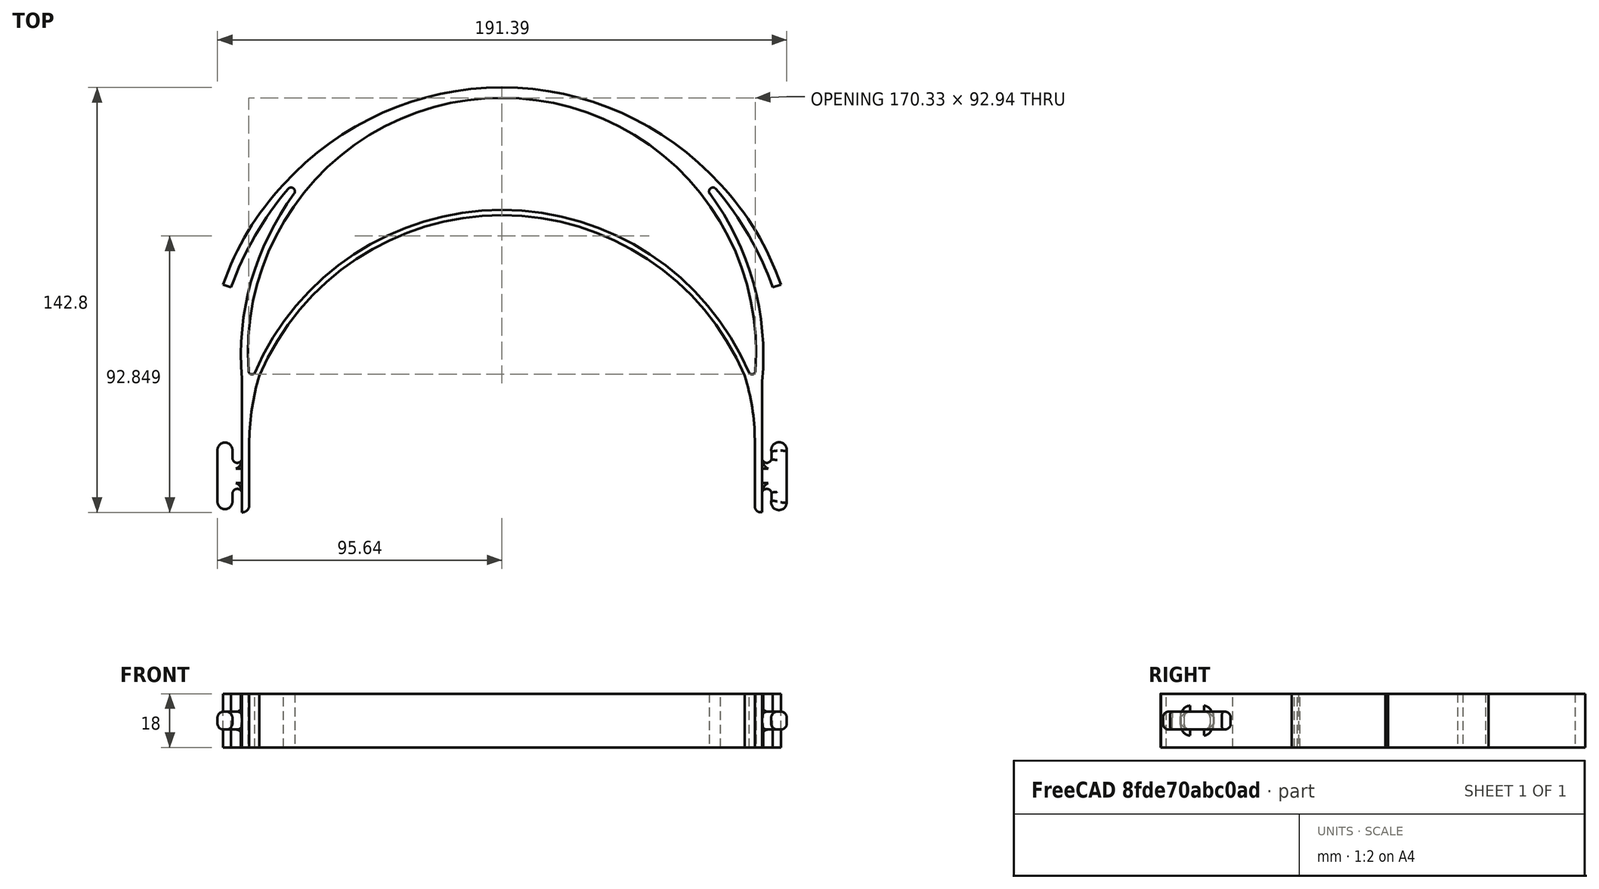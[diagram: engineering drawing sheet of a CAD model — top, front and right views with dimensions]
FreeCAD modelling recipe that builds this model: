
FCSTD DOCUMENT  (FreeCAD 0.18RUnknown)
Label: facemask
License: All rights reserved
LicenseURL: http://en.wikipedia.org/wiki/All_rights_reserved
objects: PartDesign::Fillet×3, Sketcher::SketchObject×2, PartDesign::Pad×2, Mesh::Feature×1, PartDesign::Body×1, App::Part×1
note: 10 computed .brp shape members not serialized (recipe doc carries the construction recipe); baked Part::Feature solids carry a one-line shape summary decoded from their .brp

FEATURE [Mesh::Feature] covid19_headband_rc3
  Placement = pos=(7.8,0,3) rot=(0,0,1;0rad)
FEATURE [Sketcher::SketchObject] Sketch
  sketch-geometry (26):
    g0: ArcOfCircle CenterX=1.5e-15 CenterY=-62.6202 CenterZ=0 NormalX=0 NormalY=0 NormalZ=1 AngleXU=0 Radius=88.7057 StartAngle=0.403137 EndAngle=2.73846
    g1: ArcOfCircle CenterX=0 CenterY=-19.8641 CenterZ=0 NormalX=0 NormalY=0 NormalZ=1 AngleXU=0 Radius=85.4151 StartAngle=6.20691 EndAngle=9.50106
    g2: ArcOfCircle CenterX=1.04e-14 CenterY=-29.9732 CenterZ=0 NormalX=0 NormalY=0 NormalZ=1 AngleXU=0 Radius=99 StartAngle=0.735189 EndAngle=2.4064
    g3: ArcOfCircle CenterX=1.5e-15 CenterY=-62.6202 CenterZ=0 NormalX=0 NormalY=0 NormalZ=1 AngleXU=0 Radius=90.4905 StartAngle=0.405729 EndAngle=2.73586
    g4: ArcOfCircle CenterX=-4.73373 CenterY=-28.0271 CenterZ=0 NormalX=0 NormalY=0 NormalZ=1 AngleXU=0 Radius=94.1996 StartAngle=2.38802 EndAngle=2.80895
    g5: ArcOfCircle CenterX=9.97979 CenterY=-34.403 CenterZ=0 NormalX=0 NormalY=0 NormalZ=1 AngleXU=0 Radius=107.324 StartAngle=2.43909 EndAngle=2.79722
    g6: LineSegment StartX=-93.7694 StartY=2.73342 StartZ=0 EndX=-91.0433 EndY=1.83043 EndZ=0
    g7: ArcOfCircle CenterX=4.73373 CenterY=-28.0271 CenterZ=0 NormalX=0 NormalY=0 NormalZ=1 AngleXU=0 Radius=94.1996 StartAngle=0.332648 EndAngle=0.753573
    g8: ArcOfCircle CenterX=-9.97979 CenterY=-34.403 CenterZ=0 NormalX=0 NormalY=0 NormalZ=1 AngleXU=0 Radius=107.324 StartAngle=0.344373 EndAngle=0.702501
    g9: LineSegment StartX=93.7694 StartY=2.73342 StartZ=0 EndX=91.0433 EndY=1.83043 EndZ=0
    g10: ArcOfCircle CenterX=-84.0634 CenterY=-26.2889 CenterZ=0 NormalX=0 NormalY=0 NormalZ=1 AngleXU=0 Radius=1.10656 StartAngle=3.21787 EndAngle=5.69299
    g11: ArcOfCircle CenterX=84.0634 CenterY=-26.2889 CenterZ=0 NormalX=0 NormalY=0 NormalZ=1 AngleXU=0 Radius=1.10656 StartAngle=3.73179 EndAngle=6.20691
    g12: ArcOfCircle CenterX=3.64266 CenterY=-21.0219 CenterZ=0 NormalX=0 NormalY=0 NormalZ=1 AngleXU=0 Radius=91.4037 StartAngle=2.50512 EndAngle=3.22721
    g13: ArcOfCircle CenterX=-3.52535 CenterY=-21.1802 CenterZ=0 NormalX=0 NormalY=0 NormalZ=1 AngleXU=0 Radius=91.4037 StartAngle=6.18974 EndAngle=6.92181
    g14: ArcOfCircle CenterX=-70.9258 CenterY=34.0894 CenterZ=0 NormalX=0 NormalY=0 NormalZ=1 AngleXU=0 Radius=1.32007 StartAngle=5.64672 EndAngle=8.72228
    g15: ArcOfCircle CenterX=70.9258 CenterY=34.0894 CenterZ=0 NormalX=0 NormalY=0 NormalZ=1 AngleXU=0 Radius=1.32007 StartAngle=0.702501 EndAngle=3.77806
    g16: LineSegment StartX=-87.4263 StartY=-28.8376 StartZ=0 EndX=-87.4263 EndY=-67.5348 EndZ=0
    g17: LineSegment StartX=-87.4263 StartY=-67.5348 StartZ=0 EndX=-87.4263 EndY=-73.7695 EndZ=0
    g18: ArcOfCircle CenterX=-2.80057 CenterY=-51.2587 CenterZ=0 NormalX=0 NormalY=0 NormalZ=1 AngleXU=0 Radius=82.2061 StartAngle=2.85247 EndAngle=3.11992
    g19: ArcOfCircle CenterX=-87.3497 CenterY=-71.3391 CenterZ=0 NormalX=0 NormalY=0 NormalZ=1 AngleXU=0 Radius=2.43161 StartAngle=4.68088 EndAngle=6.04379
    g20: LineSegment StartX=-84.9874 StartY=-49.4774 StartZ=0 EndX=-84.9874 EndY=-71.9157 EndZ=0
    g21: LineSegment StartX=87.4795 StartY=-29.7095 StartZ=0 EndX=87.4795 EndY=-67.711 EndZ=0
    g22: LineSegment StartX=84.9874 StartY=-49.4774 StartZ=0 EndX=84.9874 EndY=-71.9157 EndZ=0
    g23: ArcOfCircle CenterX=11.8888 CenterY=-49.8349 CenterZ=0 NormalX=0 NormalY=0 NormalZ=1 AngleXU=0 Radius=73.0994 StartAngle=0.0048912 EndAngle=0.305907
    g24: LineSegment StartX=87.4795 StartY=-67.711 StartZ=0 EndX=87.4795 EndY=-73.6987 EndZ=0
    g25: ArcOfCircle CenterX=86.9876 CenterY=-71.7531 CenterZ=0 NormalX=0 NormalY=0 NormalZ=1 AngleXU=0 Radius=2.00681 StartAngle=3.22268 EndAngle=4.96003
  constraints (50):
    c: Coincident(g0,g3)
    c: PointOnObject(g1,g-2)
    c: Radius(g2) = 99
    c: Symmetric(g2,g2,g-2)
    c: Coincident(g4,g2)
    c: Coincident(g6,g4)
    c: Coincident(g6,g5)
    c: Coincident(g7,g2)
    c: Coincident(g9,g8)
    c: Equal(g9,g6)
    c: Equal(g5,g8)
    c: Equal(g7,g4)
    c: Symmetric(g5,g8,g-2)
    c: Coincident(g7,g9)
    c: Symmetric(g5,g8,g-2)
    c: Symmetric(g3,g3,g-2)
    c: Symmetric(g0,g0,g-2)
    c: Tangent(g10,g1) = -1.5708
    c: Tangent(g11,g1) = -1.5708
    c: Symmetric(g13,g12,g-2)
    c: Tangent(g14,g5) = -1.5708
    c: Tangent(g14,g12) = 1.5708
    c: Coincident(g15,g8)
    c: Coincident(g15,g13)
    c: Equal(g14,g15)
    c: Symmetric(g4,g7,g-2)
    c: Equal(g11,g10)
    c: Equal(g13,g12)
    c: Coincident(g16,g12)
    c: Vertical(g16)
    c: Vertical(g17)
    c: Coincident(g18,g0)
    c: Coincident(g19,g17)
    c: Coincident(g20,g18)
    c: Coincident(g20,g19)
    c: Vertical(g20)
    c: Coincident(g21,g13)
    c: Vertical(g21)
    c: Vertical(g22)
    c: Coincident(g10,g3)
    c: Coincident(g11,g3)
    c: Equal(g20,g22)
    c: Symmetric(g18,g22,g-2)
    c: Coincident(g23,g0)
    c: Coincident(g23,g22)
    c: Vertical(g24)
    c: Coincident(g25,g24)
    c: Coincident(g25,g22)
    c: Coincident(g17,g16)
    c: Coincident(g24,g21)
FEATURE [PartDesign::Pad] Pad
  Length = 18
  Length2 = 100
  Midplane = true
  Profile = -> Sketch
  Type = 0
FEATURE [Sketcher::SketchObject] Sketch001
  sketch-geometry (16):
    g0: LineSegment StartX=-95.64 StartY=-52.8119 StartZ=0 EndX=-95.64 EndY=-70.2081 EndZ=0
    g1: LineSegment StartX=-90.64 StartY=-67.51 StartZ=0 EndX=-90.64 EndY=-70.2081 EndZ=0
    g2: ArcOfCircle CenterX=-89.01 CenterY=-67.51 CenterZ=0 NormalX=0 NormalY=0 NormalZ=1 AngleXU=0 Radius=1.63 StartAngle=4.87594e-08 EndAngle=3.14159
    g3: ArcOfCircle CenterX=-93.14 CenterY=-70.2081 CenterZ=0 NormalX=0 NormalY=0 NormalZ=1 AngleXU=0 Radius=2.5 StartAngle=3.14159 EndAngle=6.28319
    g4: ArcOfCircle CenterX=-93.14 CenterY=-52.8119 CenterZ=0 NormalX=0 NormalY=0 NormalZ=1 AngleXU=0 Radius=2.5 StartAngle=-9e-16 EndAngle=3.14159
    g5: ArcOfCircle CenterX=-89.01 CenterY=-55.51 CenterZ=0 NormalX=0 NormalY=0 NormalZ=1 AngleXU=0 Radius=1.63 StartAngle=3.14159 EndAngle=6.28319
    g6: LineSegment StartX=-90.64 StartY=-52.8119 StartZ=0 EndX=-90.64 EndY=-55.51 EndZ=0
    g7: LineSegment StartX=95.7222 StartY=-53.1573 StartZ=0 EndX=95.7222 EndY=-70.5535 EndZ=0
    g8: LineSegment StartX=90.575 StartY=-53.2678 StartZ=0 EndX=90.575 EndY=-55.9659 EndZ=0
    g9: LineSegment StartX=90.5881 StartY=-67.102 StartZ=0 EndX=90.5881 EndY=-69.8001 EndZ=0
    g10: ArcOfCircle CenterX=89.01 CenterY=-67.51 CenterZ=0 NormalX=0 NormalY=0 NormalZ=1 AngleXU=0 Radius=1.63 StartAngle=0.253014 EndAngle=3.14159
    g11: ArcOfCircle CenterX=89.01 CenterY=-55.51 CenterZ=0 NormalX=0 NormalY=0 NormalZ=1 AngleXU=0 Radius=1.63 StartAngle=3.14159 EndAngle=5.99972
    g12: ArcOfCircle CenterX=93.14 CenterY=-52.8119 CenterZ=0 NormalX=0 NormalY=0 NormalZ=1 AngleXU=0 Radius=2.60524 StartAngle=6.15021 EndAngle=9.60067
    g13: ArcOfCircle CenterX=93.121 CenterY=-70.4099 CenterZ=0 NormalX=0 NormalY=0 NormalZ=1 AngleXU=0 Radius=2.60524 StartAngle=2.9053 EndAngle=6.22805
    g14: LineSegment StartX=-87.38 StartY=-55.51 StartZ=0 EndX=-87.38 EndY=-67.51 EndZ=0
    g15: LineSegment StartX=87.38 StartY=-55.51 StartZ=0 EndX=87.38 EndY=-67.51 EndZ=0
  constraints (43):
    c: Vertical(g0)
    c: Vertical(g1)
    c: Tangent(g4,g0) = -1.5708
    c: Vertical(g6)
    c: Tangent(g6,g4) = 1.5708
    c: Tangent(g6,g5) = -1.5708
    c: Tangent(g3,g0) = -1.5708
    c: Tangent(g3,g1) = 1.5708
    c: Tangent(g2,g1) = -1.5708
    c: Vertical(g7)
    c: Equal(g0,g7)
    c: Vertical(g8)
    c: Vertical(g9)
    c: Coincident(g10,g9)
    c: Coincident(g11,g8)
    c: Coincident(g12,g7)
    c: Coincident(g12,g8)
    c: Coincident(g13,g9)
    c: Coincident(g13,g7)
    c: Equal(g8,g9)
    c: Equal(g6,g1)
    c: Equal(g6,g8)
    c: Symmetric(g12,g4,g-2)
    c: Symmetric(g5,g11,g-2)
    c: Symmetric(g10,g2,g-2)
    c: Coincident(g14,g5)
    c: Coincident(g14,g2)
    c: Vertical(g14)
    c: Coincident(g15,g11)
    c: Coincident(g15,g10)
    c: Vertical(g15)
    c: Tangent(g15,g11)
    c: Equal(g12,g13)
    c: Equal(g3,g4)
    c: Equal(g14,g15)
    c: DistanceX(g5,g11) = 174.76
    c: DistanceY(g5,g-1) = 55.51
    c: Radius(g4) = 2.5
    c: DistanceY(g14,g14) = 12
    c: Equal(g2,g5)
    c: Equal(g5,g11)
    c: Equal(g11,g10)
    c: Radius(g11) = 1.63
FEATURE [PartDesign::Pad] Pad001
  BaseFeature = -> Pad
  Length = 6
  Length2 = 100
  Midplane = true
  Profile = -> Sketch001
  Type = 0
FEATURE [PartDesign::Fillet] Fillet
  Base = -> Pad001 [Face34]
  BaseFeature = -> Pad001
  Radius = 2
FEATURE [PartDesign::Fillet] Fillet001
  Base = -> Fillet [Face49]
  BaseFeature = -> Fillet
  Radius = 2
FEATURE [PartDesign::Fillet] Fillet002
  Base = -> Fillet001 [Face50,Face4]
  BaseFeature = -> Fillet001
  Radius = 2
FEATURE [PartDesign::Body] Body
  Group = -> [Sketch,Pad,Sketch001,Pad001,Fillet,Fillet001,Fillet002]
  Origin = -> Origin001
  Tip = -> Fillet002
FEATURE [App::Part] Part
  Group = -> [Body]
  Origin = -> Origin
